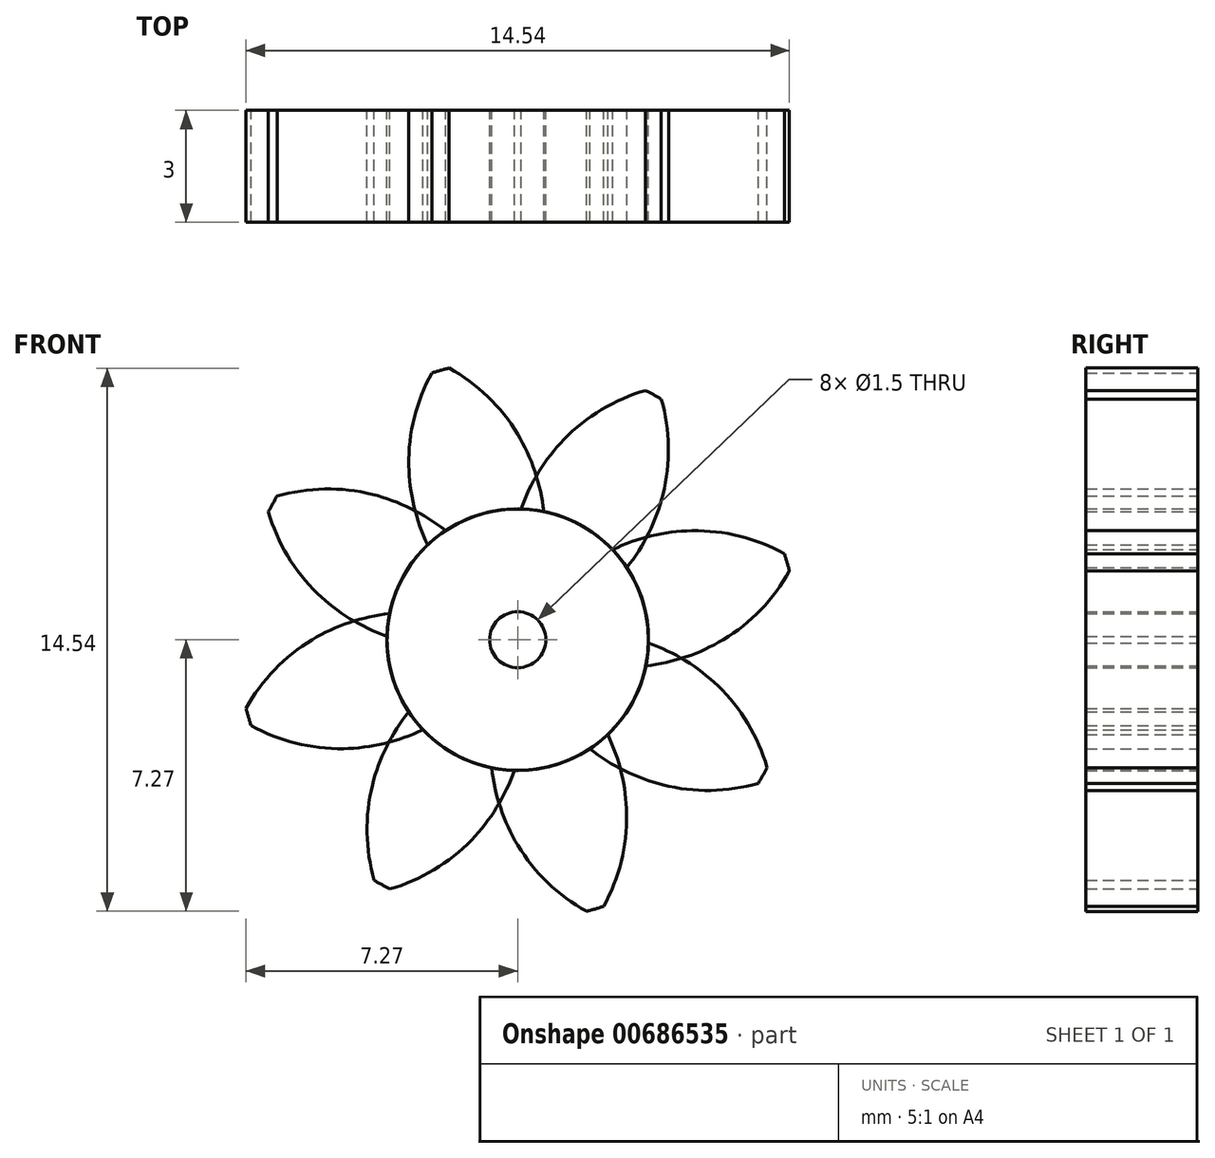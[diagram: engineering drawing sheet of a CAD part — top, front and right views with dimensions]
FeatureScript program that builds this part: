
annotation { "Feature Type Name" : "Feature", "Feature Type Description" : "" }
export const myFeature = defineFeature(function(context is Context, id is Id, definition is map)
    precondition{}
    {
        {
            var Q0;
            Q0=qCreatedBy(makeId("Front.planeOp"),FACE);
            var sketch = newSketch(context, id + "F0", { "sketchPlane" : qUnion([Q0])});
            skCircle(sketch, "E0", {"center": v(0, 0) * mm, "radius": 7.5 * mm, "construction": true});
            skCircle(sketch, "E1", {"center": v(0, 0) * mm, "radius": 5.5 * mm, "construction": true});
            skCircle(sketch, "E2", {"center": v(0, 0) * mm, "radius": 3.5 * mm});
            skLineSegment(sketch, "E3", {"start": v(0, 5.5) * mm, "end": v(-15.71, 5.5) * mm, "construction": true});
            skLineSegment(sketch, "E4", {"start": v(0, 5.5) * mm, "end": v(-16.24, -0.41) * mm, "construction": true});
            skCircle(sketch, "E5", {"center": v(0, 0) * mm, "radius": 5.17 * mm, "construction": true});
            skCircle(sketch, "E6", {"center": v(0, 5.5) * mm, "radius": 5 * mm, "construction": true});
            skPoint(sketch, "E7", {"position": v(-1.84, 7.27) * mm});
            skPoint(sketch, "E8", {"position": v(-2.07, 7.2) * mm});
            skLineSegment(sketch, "E9", {"start": v(0, 0) * mm, "end": v(-3.12, 10.88) * mm, "construction": true});
            skArc(sketch, "E10", {"start": v(0, 5.5) * mm, "mid": v(-0.8, 6.5) * mm, "end": v(-1.84, 7.27) * mm});
            skArc(sketch, "E11", {"start": v(0.7, 3.43) * mm, "mid": v(0.46, 4.5) * mm, "end": v(0, 5.5) * mm});
            skArc(sketch, "E12.MirrorCS", {"start": v(-2.92, 4.66) * mm, "mid": v(-2.77, 5.94) * mm, "end": v(-2.3, 7.14) * mm});
            skArc(sketch, "E13.MirrorCS", {"start": v(-2.41, 2.54) * mm, "mid": v(-2.78, 3.57) * mm, "end": v(-2.92, 4.66) * mm});
            skArc(sketch, "E14", {"start": v(-1.84, 7.27) * mm, "mid": v(-2.07, 7.2) * mm, "end": v(-2.3, 7.14) * mm});
            skCircle(sketch, "E15", {"center": v(0, 0) * mm, "radius": 0.75 * mm});
            skSolve(sketch);
        }
        {
            var Q0;
            {var subQ0=sQuery(id+"F0.wireOp",EDGE,"E2");var subQ1=makeQuery(id+"F0.imprint","INTERSECT",VERTEX,{"derivedFrom":[subQ0,sQuery(id+"F0.wireOp",EDGE,"E11")]});Q0=makeQuery(id+"F0.imprint","IMPRINT",FACE,{"disambiguationData":[TD([[makeQuery(id+"F0.imprint","IMPRINT",EDGE,{"disambiguationData":[TD([[subQ1,-1.0]])],"derivedFrom":subQ0}),1.0]])]});}
            var Q1;
            Q1=makeQuery(id+"F0.imprint","IMPRINT",FACE,{"disambiguationData":[TD([[makeQuery(id+"F0.imprint","IMPRINT",EDGE,{"derivedFrom":sQuery(id+"F0.wireOp",EDGE,"E10")}),1.0]])]});
            extrude(context, id + "F1", {"entities" : qUnion([Q0, Q1]), "depth" : 3 * mm, "offsetDistance" : 25 * mm});
        }
        {
            var Q0;
            Q0=makeQuery(id+"F1.opExtrude","SWEPT_BODY",BODY,{"disambiguationData":[OSD([sQuery(id+"F0.wireOp",EDGE,"E2"),sQuery(id+"F0.wireOp",EDGE,"E10"),sQuery(id+"F0.wireOp",EDGE,"E11"),sQuery(id+"F0.wireOp",EDGE,"E12.MirrorCS"),sQuery(id+"F0.wireOp",EDGE,"E13.MirrorCS"),sQuery(id+"F0.wireOp",EDGE,"E14")])]});
            var Q1;
            Q1=makeQuery(id+"F1.opExtrude","SWEPT_FACE",FACE,{"disambiguationData":[OSD([sQuery(id+"F0.wireOp",EDGE,"E2")])]});
            circularPattern(context, id + "F2", {"entities" : qUnion([Q0]), "axis" : qUnion([Q1]), "angle" : 360 * degree, "instanceCount" : 8, "equalSpace" : true});
        }
    });
